# Revit family: Stowmate_WM_BagTrac_Linc
name_source: partatom
category: Specialty Equipment
units: mm (PartAtom-declared; Revit-internal decimal feet)

## family parameters
Cut with Voids When Loaded = No
Part Type = Normal
Room Calculation Point = No
Round Connector Dimension = Use Diameter
Shared = No

## types (3) — shared parameters
JoinerSpacing = 3000 mm  [stored 9.84252 ft]
JoinerSpacingCalculated = 3004 mm  [stored 9.85564 ft]
JoinerTeeSectionThickness = 4 mm  [stored 0.0131234 ft]
Manufacturer = Linc Furniture
Model = Safehook
Revision = 20230725
URL = https://lincfurniture.com.au

## per-type parameters (varying)
| type | Description | HookType | Type Comments |
| Euro V2 Bag Hook | Stowmate WM BagTrac with Euro V2 Bag Hooks | Safehook_Linc : Euro V2 Bag Hook | Stowmate WM BagTrac with Euro V2 Bag Hooks |
| Ihook Mk2 Bag Hook | Stowmate WM BagTrac with IHook Mk2 Bag Hooks | Safehook_Linc : Ihook Mk2 Bag Hook | Stowmate WM BagTrac with IHook Mk2 Bag Hooks |
| OZIhook Bag Hook | Stowmate WM BagTrac with OZIhook Bag Hooks | Safehook_Linc : OZIhook Bag Hook | Stowmate WM BagTrac with OZIhook Bag Hooks |

note: [stored X ft] marks values corroborated as IEEE doubles in the binary element streams (Revit-internal decimal feet)

## geometry (parser evidence)
native form markers: Revolve x1, Sweep x22
no freeform markers — native parametric forms only
